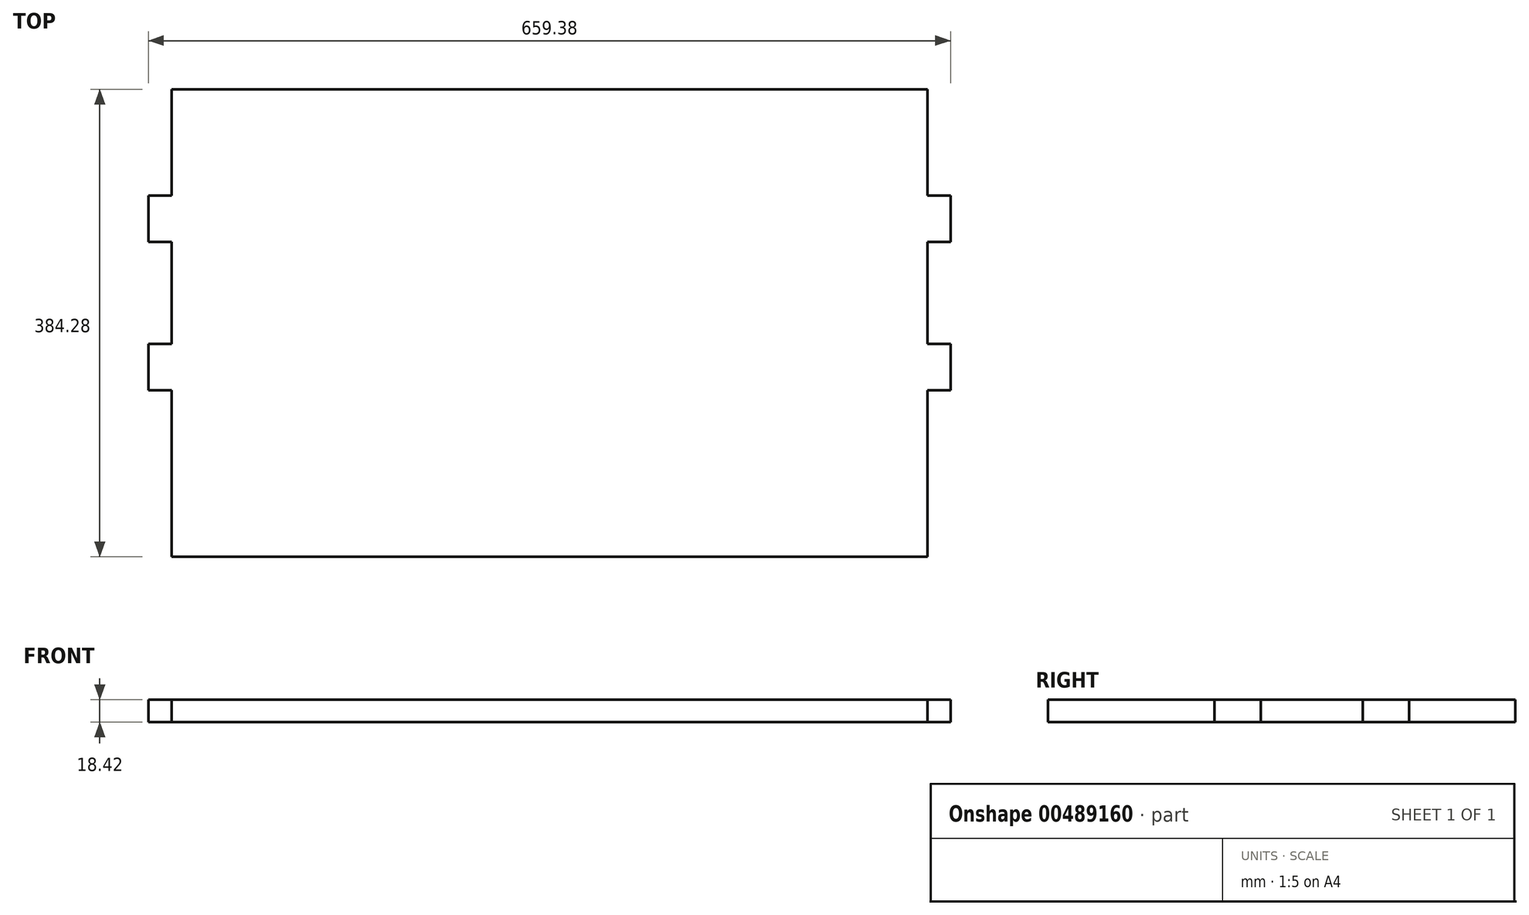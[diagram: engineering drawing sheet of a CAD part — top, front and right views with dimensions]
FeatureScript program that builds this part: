
annotation { "Feature Type Name" : "Feature", "Feature Type Description" : "" }
export const myFeature = defineFeature(function(context is Context, id is Id, definition is map)
    precondition{}
    {
        {
            var Q0;
            Q0=qCreatedBy(makeId("Top.planeOp"),FACE);
            var sketch = newSketch(context, id + "F0", { "sketchPlane" : qUnion([Q0])});
            skLineSegment(sketch, "E0", {"start": v(0, 0) * mm, "end": v(0, 136.8) * mm});
            skLineSegment(sketch, "E1", {"start": v(0, 136.8) * mm, "end": v(-19.05, 136.8) * mm});
            skLineSegment(sketch, "E2", {"start": v(-19.05, 136.8) * mm, "end": v(-19.05, 174.9) * mm});
            skLineSegment(sketch, "E3", {"start": v(-19.05, 174.9) * mm, "end": v(0, 174.9) * mm});
            skLineSegment(sketch, "E4", {"start": v(0, 174.9) * mm, "end": v(0, 258.72) * mm});
            skLineSegment(sketch, "E5", {"start": v(0, 258.72) * mm, "end": v(-19.05, 258.72) * mm});
            skLineSegment(sketch, "E6", {"start": v(-19.05, 258.72) * mm, "end": v(-19.05, 296.82) * mm});
            skLineSegment(sketch, "E7", {"start": v(-19.05, 296.82) * mm, "end": v(0, 296.82) * mm});
            skLineSegment(sketch, "E8", {"start": v(0, 296.82) * mm, "end": v(0, 384.28) * mm});
            skLineSegment(sketch, "E9", {"start": v(0, 384.28) * mm, "end": v(621.28, 384.28) * mm});
            skLineSegment(sketch, "E10", {"start": v(621.28, 384.28) * mm, "end": v(621.28, 296.82) * mm});
            skLineSegment(sketch, "E11", {"start": v(621.28, 296.82) * mm, "end": v(640.33, 296.82) * mm});
            skLineSegment(sketch, "E12", {"start": v(640.33, 296.82) * mm, "end": v(640.33, 258.72) * mm});
            skLineSegment(sketch, "E13", {"start": v(640.33, 258.72) * mm, "end": v(621.28, 258.72) * mm});
            skLineSegment(sketch, "E14", {"start": v(621.28, 258.72) * mm, "end": v(621.28, 174.9) * mm});
            skLineSegment(sketch, "E15", {"start": v(621.28, 174.9) * mm, "end": v(640.33, 174.9) * mm});
            skLineSegment(sketch, "E16", {"start": v(640.33, 174.9) * mm, "end": v(640.33, 136.8) * mm});
            skLineSegment(sketch, "E17", {"start": v(640.33, 136.8) * mm, "end": v(621.28, 136.8) * mm});
            skLineSegment(sketch, "E18", {"start": v(621.28, 136.8) * mm, "end": v(621.28, 0) * mm});
            skLineSegment(sketch, "E19", {"start": v(621.28, 0) * mm, "end": v(0, 0) * mm});
            skSolve(sketch);
        }
        {
            var Q0;
            Q0=makeQuery(id+"F0.imprint","IMPRINT",FACE,{"disambiguationData":[TD([[makeQuery(id+"F0.imprint","IMPRINT",EDGE,{"derivedFrom":sQuery(id+"F0.wireOp",EDGE,"E0")}),-1.0]])]});
            extrude(context, id + "F1", {"entities" : qUnion([Q0]), "depth" : 18.41 * mm, "offsetDistance" : 25.4 * mm, "symmetric" : true});
        }
    });
